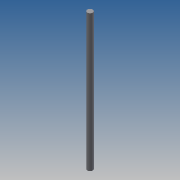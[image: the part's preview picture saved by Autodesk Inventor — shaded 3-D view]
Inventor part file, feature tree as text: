
AUTODESK INVENTOR PART (.ipt)
format: ipt  version: 2013 (Build 170138000, 138)  size: 60,928 bytes
history: native  units: mm
features: extrude x1, sketch x1
ambient origin geometry x8: Origin, YZ Plane, XZ Plane, XY Plane, X Axis, Y Axis, Z Axis, Center Point
bodies: Solid1 (feature_tree)
feature tree (2):
  extrude  "Extrusion1"  Depth=150.0mm TaperAngle=0.0deg
  sketch  "Sketch1"  dims[d0=6.0mm d2=150.0mm d3=0.0mm]
